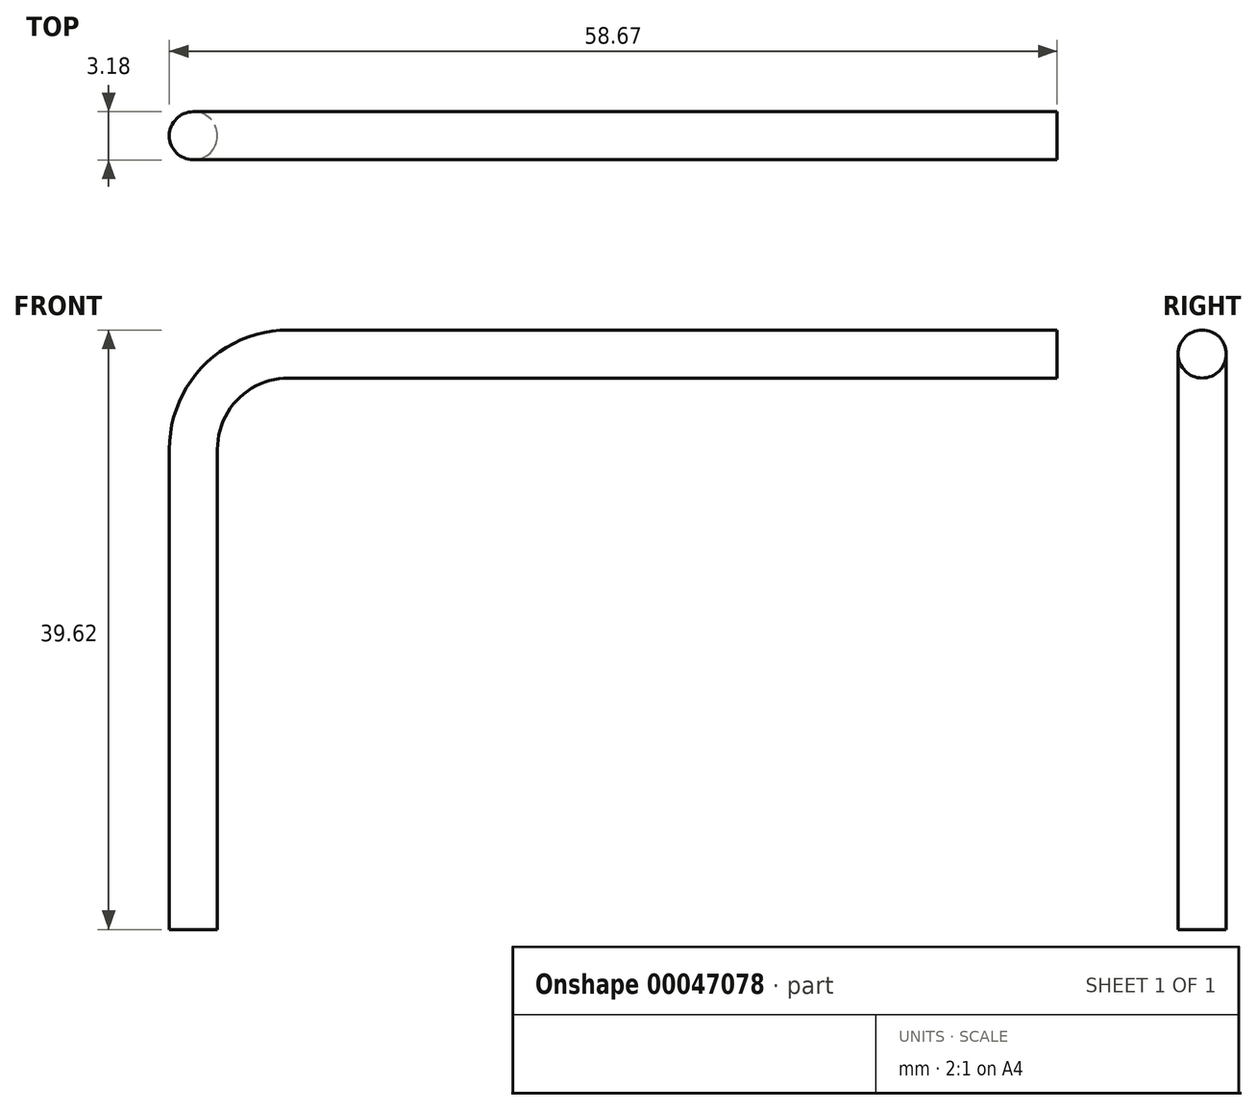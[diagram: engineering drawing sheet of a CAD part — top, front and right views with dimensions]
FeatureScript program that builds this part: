
annotation { "Feature Type Name" : "Feature", "Feature Type Description" : "" }
export const myFeature = defineFeature(function(context is Context, id is Id, definition is map)
    precondition{}
    {
        {
            var Q0;
            Q0=qCreatedBy(makeId("Front.planeOp"),FACE);
            var sketch = newSketch(context, id + "F0", { "sketchPlane" : qUnion([Q0])});
            skLineSegment(sketch, "E0", {"start": v(0, 0) * mm, "end": v(0, 31.75) * mm});
            skLineSegment(sketch, "E1", {"start": v(7.87, 39.62) * mm, "end": v(58.67, 39.62) * mm});
            skPoint(sketch, "E2.visualSharp", {"position": v(0, 39.62) * mm});
            skArc(sketch, "E2.filletArc", {"start": v(7.87, 39.62) * mm, "mid": v(2.3, 37.32) * mm, "end": v(0, 31.75) * mm});
            skSolve(sketch);
        }
        {
            var Q0;
            Q0=qCreatedBy(makeId("Top.planeOp"),FACE);
            var sketch = newSketch(context, id + "F1", { "sketchPlane" : qUnion([Q0])});
            skCircle(sketch, "E3", {"center": v(1.59, 0) * mm, "radius": 1.59 * mm});
            skSolve(sketch);
        }
        {
            var Q0;
            Q0 = qSketchRegion(id + "F1", true);
            var Q1;
            Q1 = qConstructionFilter(qBodyType(qCreatedBy(id + "F0" ,EDGE), BodyType.WIRE), ConstructionObject.NO);
            sweep(context, id + "F2", {"profiles" : qUnion([Q0]), "path" : qUnion([Q1])});
        }
    });
